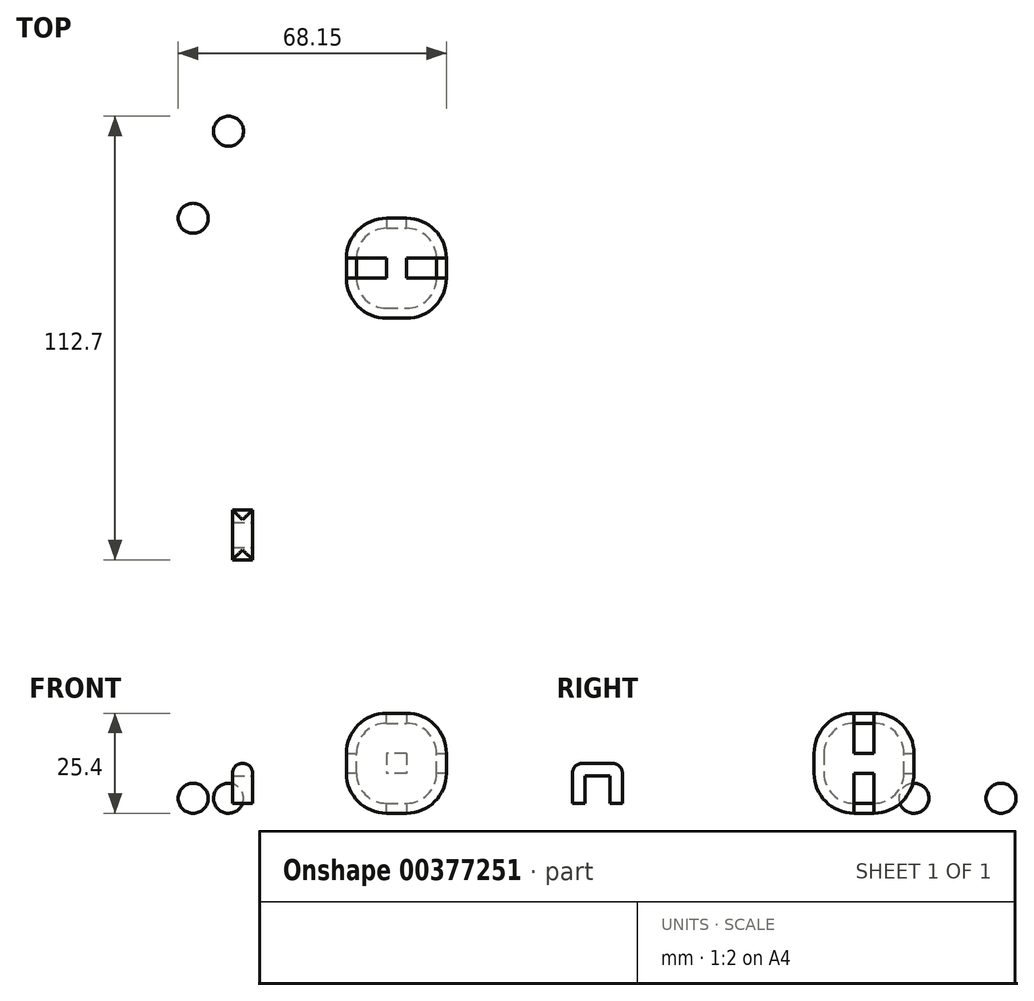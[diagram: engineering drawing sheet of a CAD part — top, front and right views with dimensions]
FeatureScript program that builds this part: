
annotation { "Feature Type Name" : "Feature", "Feature Type Description" : "" }
export const myFeature = defineFeature(function(context is Context, id is Id, definition is map)
    precondition{}
    {
        {
            var Q0;
            Q0=qCreatedBy(makeId("Top.planeOp"),FACE);
            var sketch = newSketch(context, id + "F0", { "sketchPlane" : qUnion([Q0])});
            skLineSegment(sketch, "E0.bottom", {"start": v(0, 0) * mm, "end": v(-25.4, 0) * mm});
            skLineSegment(sketch, "E0.top", {"start": v(0, 25.4) * mm, "end": v(-25.4, 25.4) * mm});
            skLineSegment(sketch, "E0.left", {"start": v(0, 0) * mm, "end": v(0, 25.4) * mm});
            skLineSegment(sketch, "E0.right", {"start": v(-25.4, 0) * mm, "end": v(-25.4, 25.4) * mm});
            skSolve(sketch);
        }
        {
            var Q0;
            Q0=makeQuery(id+"F0.imprint","IMPRINT",FACE,{"disambiguationData":[TD([[makeQuery(id+"F0.imprint","IMPRINT",EDGE,{"derivedFrom":sQuery(id+"F0.wireOp",EDGE,"E0.bottom")}),-1.0]])]});
            extrude(context, id + "F1", {"entities" : qUnion([Q0]), "depth" : 25.4 * mm});
        }
        {
            var Q0;
            Q0=makeQuery(id+"F1.opExtrude","CAP_FACE",FACE,{"disambiguationData":[OSD([sQuery(id+"F0.wireOp",EDGE,"E0.bottom"),sQuery(id+"F0.wireOp",EDGE,"E0.top"),sQuery(id+"F0.wireOp",EDGE,"E0.left"),sQuery(id+"F0.wireOp",EDGE,"E0.right")])],"isStart":false});
            var Q1;
            Q1=makeQuery(id+"F1.opExtrude","SWEPT_FACE",FACE,{"disambiguationData":[OSD([sQuery(id+"F0.wireOp",EDGE,"E0.bottom")])]});
            var Q2;
            Q2=makeQuery(id+"F1.opExtrude","SWEPT_FACE",FACE,{"disambiguationData":[OSD([sQuery(id+"F0.wireOp",EDGE,"E0.right")])]});
            var Q3;
            Q3=makeQuery(id+"F1.opExtrude","SWEPT_FACE",FACE,{"disambiguationData":[OSD([sQuery(id+"F0.wireOp",EDGE,"E0.top")])]});
            var Q4;
            Q4=makeQuery(id+"F1.opExtrude","CAP_FACE",FACE,{"disambiguationData":[OSD([sQuery(id+"F0.wireOp",EDGE,"E0.bottom"),sQuery(id+"F0.wireOp",EDGE,"E0.top"),sQuery(id+"F0.wireOp",EDGE,"E0.left"),sQuery(id+"F0.wireOp",EDGE,"E0.right")])],"isStart":true});
            fillet(context, id + "F2", {"entities" : qUnion([Q0, Q1, Q2, Q3, Q4]), "radius" : 10.16 * mm, "tangentPropagation" : true, "allowEdgeOverflow" : false});
        }
        {
            var Q0;
            Q0=qCreatedBy(makeId("Top.planeOp"),FACE);
            var sketch = newSketch(context, id + "F3", { "sketchPlane" : qUnion([Q0])});
            skLineSegment(sketch, "E1.bottom", {"start": v(-54.34, -48.68) * mm, "end": v(-49.26, -48.68) * mm});
            skLineSegment(sketch, "E1.top", {"start": v(-54.34, -61.38) * mm, "end": v(-49.26, -61.38) * mm});
            skLineSegment(sketch, "E1.left", {"start": v(-54.34, -48.68) * mm, "end": v(-54.34, -61.38) * mm});
            skLineSegment(sketch, "E1.right", {"start": v(-49.26, -48.68) * mm, "end": v(-49.26, -61.38) * mm});
            skSolve(sketch);
        }
        {
            var Q0;
            Q0=makeQuery(id+"F3.imprint","IMPRINT",FACE,{"disambiguationData":[TD([[makeQuery(id+"F3.imprint","IMPRINT",EDGE,{"derivedFrom":sQuery(id+"F3.wireOp",EDGE,"E1.bottom")}),-1.0]])]});
            extrude(context, id + "F4", {"entities" : qUnion([Q0]), "depth" : 12.7 * mm});
        }
        {
            var Q0;
            Q0=makeQuery(id+"F4.opExtrude","SWEPT_FACE",FACE,{"disambiguationData":[OSD([sQuery(id+"F3.wireOp",EDGE,"E1.right")])]});
            var sketch = newSketch(context, id + "F5", { "sketchPlane" : qUnion([Q0])});
            skLineSegment(sketch, "E2", {"start": v(-55.03, 0) * mm, "end": v(-61.38, 0) * mm});
            skLineSegment(sketch, "E3", {"start": v(-61.38, 0) * mm, "end": v(-58.2, 0) * mm});
            skLineSegment(sketch, "E4", {"start": v(-58.2, 0) * mm, "end": v(-58.2, 9.53) * mm});
            skLineSegment(sketch, "E5", {"start": v(-58.2, 9.53) * mm, "end": v(-58.2, 0) * mm});
            skLineSegment(sketch, "E6", {"start": v(-55.03, 0) * mm, "end": v(-48.68, 0) * mm});
            skLineSegment(sketch, "E7", {"start": v(-48.68, 0) * mm, "end": v(-51.86, 0) * mm});
            skLineSegment(sketch, "E8", {"start": v(-51.86, 0) * mm, "end": v(-51.86, 9.53) * mm});
            skLineSegment(sketch, "E9", {"start": v(-51.86, 12.7) * mm, "end": v(-61.38, 12.7) * mm});
            skLineSegment(sketch, "E10", {"start": v(-61.38, 12.7) * mm, "end": v(-61.38, 6.35) * mm});
            skLineSegment(sketch, "E11", {"start": v(-48.68, 6.35) * mm, "end": v(-48.68, 12.7) * mm});
            skLineSegment(sketch, "E12", {"start": v(-48.68, 12.7) * mm, "end": v(-48.68, 9.53) * mm});
            skLineSegment(sketch, "E13", {"start": v(-51.86, 9.53) * mm, "end": v(-58.2, 9.53) * mm});
            skPoint(sketch, "E14.orphan", {"position": v(-61.38, 9.53) * mm});
            skSolve(sketch);
        }
        {
            var Q0;
            Q0=makeQuery(id+"F5.imprint","IMPRINT",FACE,{"disambiguationData":[TD([[makeQuery(id+"F5.imprint","IMPRINT",EDGE,{"derivedFrom":sQuery(id+"F5.wireOp",EDGE,"E2")}),-1.0]])]});
            extrude(context, id + "F6", {"entities" : qUnion([Q0]), "operationType" : NewBodyOperationType.REMOVE, "oppositeDirection" : true, "depth" : 5.08 * mm});
        }
        {
            var Q0;
            Q0=makeQuery(id+"F4.opExtrude","CAP_EDGE",EDGE,{"disambiguationData":[OSD([sQuery(id+"F3.wireOp",EDGE,"E1.bottom")])],"isStart":false});
            var Q1;
            Q1=makeQuery(id+"F4.opExtrude","CAP_EDGE",EDGE,{"disambiguationData":[OSD([sQuery(id+"F3.wireOp",EDGE,"E1.top")])],"isStart":false});
            var Q2;
            Q2=makeQuery(id+"F6.boolean.opBoolean","COPY",EDGE,{"derivedFrom":makeQuery(id+"F6.opExtrude","CAP_EDGE",EDGE,{"disambiguationData":[OSD([sQuery(id+"F5.wireOp",EDGE,"E13")])],"isStart":true})});
            var Q3;
            Q3=makeQuery(id+"F6.boolean.opBoolean","COPY",EDGE,{"derivedFrom":makeQuery(id+"F6.opExtrude","CAP_EDGE",EDGE,{"disambiguationData":[OSD([sQuery(id+"F5.wireOp",EDGE,"E5")])],"isStart":true})});
            var Q4;
            Q4=makeQuery(id+"F6.boolean.opBoolean","COPY",EDGE,{"derivedFrom":makeQuery(id+"F6.opExtrude","CAP_EDGE",EDGE,{"disambiguationData":[OSD([sQuery(id+"F5.wireOp",EDGE,"E8")])],"isStart":true})});
            var Q5;
            Q5=makeQuery(id+"F6.boolean.opBoolean","COPY",EDGE,{"derivedFrom":makeQuery(id+"F6.opExtrude","CAP_EDGE",EDGE,{"disambiguationData":[OSD([sQuery(id+"F5.wireOp",EDGE,"E13")])],"isStart":false})});
            var Q6;
            Q6=makeQuery(id+"F6.boolean.opBoolean","COPY",EDGE,{"derivedFrom":makeQuery(id+"F6.opExtrude","CAP_EDGE",EDGE,{"disambiguationData":[OSD([sQuery(id+"F5.wireOp",EDGE,"E8")])],"isStart":false})});
            var Q7;
            Q7=makeQuery(id+"F6.boolean.opBoolean","COPY",EDGE,{"derivedFrom":makeQuery(id+"F6.opExtrude","CAP_EDGE",EDGE,{"disambiguationData":[OSD([sQuery(id+"F5.wireOp",EDGE,"E5")])],"isStart":false})});
            var Q8;
            Q8=makeQuery(id+"F4.opExtrude","CAP_EDGE",EDGE,{"disambiguationData":[OSD([sQuery(id+"F3.wireOp",EDGE,"E1.left")])],"isStart":false});
            var Q9;
            Q9=makeQuery(id+"F4.opExtrude","CAP_EDGE",EDGE,{"disambiguationData":[OSD([sQuery(id+"F3.wireOp",EDGE,"E1.right")])],"isStart":false});
            fillet(context, id + "F7", {"entities" : qUnion([Q0, Q1, Q2, Q3, Q4, Q5, Q6, Q7, Q8, Q9]), "radius" : 2.54 * mm, "tangentPropagation" : true, "allowEdgeOverflow" : false});
        }
        {
            var Q0;
            Q0=makeQuery(id+"F1.opExtrude","SWEPT_FACE",FACE,{"disambiguationData":[OSD([sQuery(id+"F0.wireOp",EDGE,"E0.top")])]});
            var Q1;
            {var subQ0=sQuery(id+"F0.wireOp",EDGE,"E0.left");Q1=makeQuery(id+"F2.opFillet","BLEND_FACE",FACE,{"disambiguationData":[OSD([subQ0]),TDD([makeQuery(id+"F1.opExtrude","CAP_EDGE",EDGE,{"disambiguationData":[OSD([subQ0])],"isStart":false})])]});}
            var Q2;
            {var subQ0=sQuery(id+"F0.wireOp",EDGE,"E0.left");Q2=makeQuery(id+"F2.opFillet","BLEND_FACE",FACE,{"disambiguationData":[OSD([subQ0]),TDD([makeQuery(id+"F1.opExtrude","CAP_EDGE",EDGE,{"disambiguationData":[OSD([subQ0])],"isStart":true})])]});}
            var Q3;
            {var subQ0=sQuery(id+"F0.wireOp",EDGE,"E0.right");Q3=makeQuery(id+"F2.opFillet","BLEND_FACE",FACE,{"disambiguationData":[OSD([subQ0]),TDD([makeQuery(id+"F1.opExtrude","CAP_EDGE",EDGE,{"disambiguationData":[OSD([subQ0])],"isStart":false})])]});}
            var Q4;
            {var subQ0=sQuery(id+"F0.wireOp",EDGE,"E0.right");Q4=makeQuery(id+"F2.opFillet","BLEND_FACE",FACE,{"disambiguationData":[OSD([subQ0]),TDD([makeQuery(id+"F1.opExtrude","CAP_EDGE",EDGE,{"disambiguationData":[OSD([subQ0])],"isStart":true})])]});}
            shell(context, id + "F8", {"entities" : qUnion([Q0, Q1, Q2, Q3, Q4]), "thickness" : 2.54 * mm});
        }
        {
            var Q0;
            Q0=qCreatedBy(makeId("Top.planeOp"),FACE);
            var sketch = newSketch(context, id + "F9", { "sketchPlane" : qUnion([Q0])});
            skLineSegment(sketch, "E15.bottom", {"start": v(-51.56, 43.7) * mm, "end": v(-59.18, 43.7) * mm});
            skLineSegment(sketch, "E15.top", {"start": v(-51.56, 51.32) * mm, "end": v(-59.18, 51.32) * mm});
            skLineSegment(sketch, "E15.left", {"start": v(-51.56, 43.7) * mm, "end": v(-51.56, 51.32) * mm});
            skLineSegment(sketch, "E15.right", {"start": v(-59.18, 43.7) * mm, "end": v(-59.18, 51.32) * mm});
            skLineSegment(sketch, "E16.bottom", {"start": v(-60.53, 21.58) * mm, "end": v(-68.15, 21.58) * mm});
            skLineSegment(sketch, "E16.top", {"start": v(-60.53, 29.2) * mm, "end": v(-68.15, 29.2) * mm});
            skLineSegment(sketch, "E16.left", {"start": v(-60.53, 21.58) * mm, "end": v(-60.53, 29.2) * mm});
            skLineSegment(sketch, "E16.right", {"start": v(-68.15, 21.58) * mm, "end": v(-68.15, 29.2) * mm});
            skSolve(sketch);
        }
        {
            var Q0;
            Q0=makeQuery(id+"F9.imprint","IMPRINT",FACE,{"disambiguationData":[TD([[makeQuery(id+"F9.imprint","IMPRINT",EDGE,{"derivedFrom":sQuery(id+"F9.wireOp",EDGE,"E16.bottom")}),-1.0]])]});
            var Q1;
            Q1=makeQuery(id+"F9.imprint","IMPRINT",FACE,{"disambiguationData":[TD([[makeQuery(id+"F9.imprint","IMPRINT",EDGE,{"derivedFrom":sQuery(id+"F9.wireOp",EDGE,"E15.bottom")}),-1.0]])]});
            extrude(context, id + "F10", {"entities" : qUnion([Q0, Q1]), "depth" : 7.62 * mm});
        }
        {
            var Q0;
            Q0=makeQuery(id+"F10.opExtrude","SWEPT_FACE",FACE,{"disambiguationData":[OSD([sQuery(id+"F9.wireOp",EDGE,"E15.left")])]});
            var Q1;
            Q1=makeQuery(id+"F10.opExtrude","SWEPT_FACE",FACE,{"disambiguationData":[OSD([sQuery(id+"F9.wireOp",EDGE,"E15.top")])]});
            var Q2;
            Q2=makeQuery(id+"F10.opExtrude","SWEPT_FACE",FACE,{"disambiguationData":[OSD([sQuery(id+"F9.wireOp",EDGE,"E15.right")])]});
            var Q3;
            Q3=makeQuery(id+"F10.opExtrude","SWEPT_FACE",FACE,{"disambiguationData":[OSD([sQuery(id+"F9.wireOp",EDGE,"E15.bottom")])]});
            var Q4;
            Q4=makeQuery(id+"F10.opExtrude","CAP_FACE",FACE,{"disambiguationData":[OSD([sQuery(id+"F9.wireOp",EDGE,"E16.bottom"),sQuery(id+"F9.wireOp",EDGE,"E16.top"),sQuery(id+"F9.wireOp",EDGE,"E16.left"),sQuery(id+"F9.wireOp",EDGE,"E16.right")])],"isStart":true});
            var Q5;
            Q5=makeQuery(id+"F10.opExtrude","SWEPT_FACE",FACE,{"disambiguationData":[OSD([sQuery(id+"F9.wireOp",EDGE,"E16.top")])]});
            var Q6;
            Q6=makeQuery(id+"F10.opExtrude","SWEPT_FACE",FACE,{"disambiguationData":[OSD([sQuery(id+"F9.wireOp",EDGE,"E16.right")])]});
            var Q7;
            Q7=makeQuery(id+"F10.opExtrude","CAP_FACE",FACE,{"disambiguationData":[OSD([sQuery(id+"F9.wireOp",EDGE,"E16.bottom"),sQuery(id+"F9.wireOp",EDGE,"E16.top"),sQuery(id+"F9.wireOp",EDGE,"E16.left"),sQuery(id+"F9.wireOp",EDGE,"E16.right")])],"isStart":false});
            var Q8;
            Q8=makeQuery(id+"F10.opExtrude","SWEPT_FACE",FACE,{"disambiguationData":[OSD([sQuery(id+"F9.wireOp",EDGE,"E16.bottom")])]});
            fillet(context, id + "F11", {"entities" : qUnion([Q0, Q1, Q2, Q3, Q4, Q5, Q6, Q7, Q8]), "radius" : 3.8 * mm, "tangentPropagation" : true, "allowEdgeOverflow" : false});
        }
        {
            var Q0;
            {var subQ0=sQuery(id+"F3.wireOp",EDGE,"E1.top");var subQ1=sQuery(id+"F3.wireOp",EDGE,"E1.left");var subQ2=sQuery(id+"F3.wireOp",EDGE,"E1.right");Q0=makeQuery(id+"F6.boolean.opBoolean","SPLIT",FACE,{"disambiguationData":[TD([makeQuery(id+"F4.opExtrude","SWEPT_FACE",FACE,{"disambiguationData":[OSD([subQ0])]})])],"derivedFrom":makeQuery(id+"F4.opExtrude","CAP_FACE",FACE,{"disambiguationData":[OSD([sQuery(id+"F3.wireOp",EDGE,"E1.bottom"),subQ0,subQ1,subQ2])],"isStart":true})});}
            var sketch = newSketch(context, id + "F12", { "sketchPlane" : qUnion([Q0])});
            skSolve(sketch);
        }
        {
            var Q0;
            Q0 = qSketchRegion(id + "F12", true);
            var Q1;
            {var subQ0=sQuery(id+"F3.wireOp",EDGE,"E1.top");Q1=makeQuery(id+"F12.imprint","IMPRINT",FACE,{"disambiguationData":[TD([[makeQuery(id+"F12.imprint","IMPRINT",EDGE,{"derivedFrom":makeQuery(id+"F4.opExtrude","CAP_EDGE",EDGE,{"disambiguationData":[OSD([subQ0])],"isStart":true})}),-1.0]])]});}
            extrude(context, id + "F13", {"entities" : qUnion([Q0, Q1]), "operationType" : NewBodyOperationType.REMOVE, "oppositeDirection" : true, "depth" : 2.54 * mm});
        }
        {
            var Q0;
            {var subQ0=sQuery(id+"F3.wireOp",EDGE,"E1.bottom");var subQ1=sQuery(id+"F3.wireOp",EDGE,"E1.right");var subQ2=sQuery(id+"F3.wireOp",EDGE,"E1.left");Q0=makeQuery(id+"F6.boolean.opBoolean","SPLIT",FACE,{"disambiguationData":[TD([makeQuery(id+"F4.opExtrude","SWEPT_FACE",FACE,{"disambiguationData":[OSD([subQ0])]})])],"derivedFrom":makeQuery(id+"F4.opExtrude","CAP_FACE",FACE,{"disambiguationData":[OSD([subQ0,sQuery(id+"F3.wireOp",EDGE,"E1.top"),subQ2,subQ1])],"isStart":true})});}
            var sketch = newSketch(context, id + "F14", { "sketchPlane" : qUnion([Q0])});
            skSolve(sketch);
        }
        {
            var Q0;
            Q0 = qSketchRegion(id + "F14", true);
            var Q1;
            {var subQ0=sQuery(id+"F3.wireOp",EDGE,"E1.bottom");Q1=makeQuery(id+"F14.imprint","IMPRINT",FACE,{"disambiguationData":[TD([[makeQuery(id+"F14.imprint","IMPRINT",EDGE,{"derivedFrom":makeQuery(id+"F4.opExtrude","CAP_EDGE",EDGE,{"disambiguationData":[OSD([subQ0])],"isStart":true})}),1.0]])]});}
            extrude(context, id + "F15", {"entities" : qUnion([Q0, Q1]), "operationType" : NewBodyOperationType.REMOVE, "oppositeDirection" : true, "depth" : 2.54 * mm});
        }
    });
